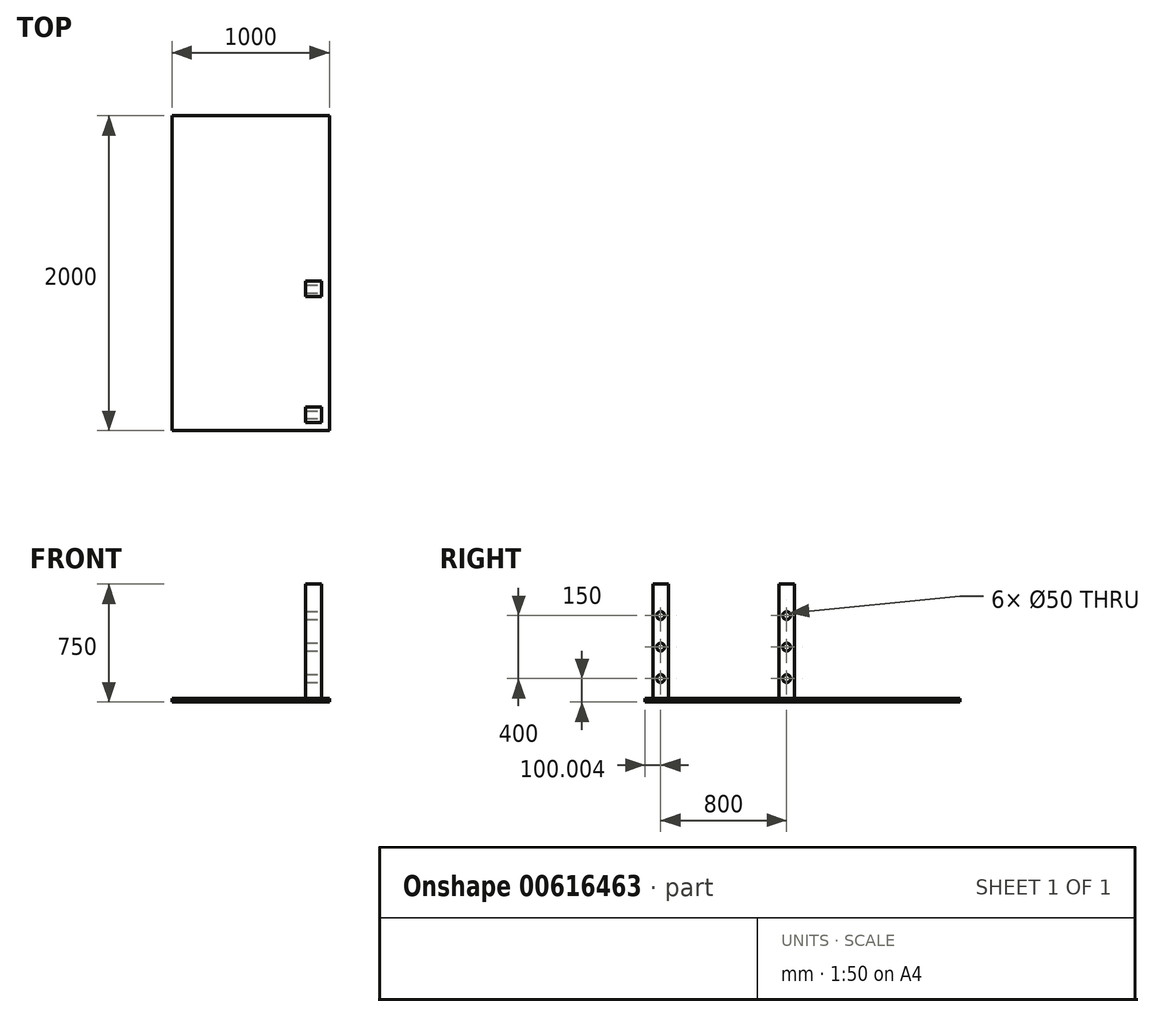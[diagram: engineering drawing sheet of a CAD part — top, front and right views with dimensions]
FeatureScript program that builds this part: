
annotation { "Feature Type Name" : "Feature", "Feature Type Description" : "" }
export const myFeature = defineFeature(function(context is Context, id is Id, definition is map)
    precondition{}
    {
        {
            var Q0;
            Q0=qCreatedBy(makeId("Top.planeOp"),FACE);
            var sketch = newSketch(context, id + "F0", { "sketchPlane" : qUnion([Q0])});
            skLineSegment(sketch, "E0.bottom", {"start": v(503.13, -1003.32) * mm, "end": v(-496.87, -1003.32) * mm});
            skLineSegment(sketch, "E0.top", {"start": v(503.13, 996.68) * mm, "end": v(-496.87, 996.68) * mm});
            skLineSegment(sketch, "E0.left", {"start": v(503.13, -1003.32) * mm, "end": v(503.13, 996.68) * mm});
            skLineSegment(sketch, "E0.right", {"start": v(-496.87, -1003.32) * mm, "end": v(-496.87, 996.68) * mm});
            skPoint(sketch, "E0.middle", {"position": v(3.13, -3.32) * mm});
            skLineSegment(sketch, "E1", {"start": v(-496.87, 996.68) * mm, "end": v(503.13, -1003.32) * mm, "construction": true});
            skSolve(sketch);
        }
        {
            var Q0;
            Q0 = qSketchRegion(id + "F0", true);
            extrude(context, id + "F1", {"entities" : qUnion([Q0]), "depth" : 25 * mm, "offsetDistance" : 25 * mm});
        }
        {
            var Q0;
            Q0=makeQuery(id+"F1.opExtrude","SWEPT_FACE",FACE,{"disambiguationData":[OSD([sQuery(id+"F0.wireOp",EDGE,"E0.left")])]});
            cPlane(context, id + "F2", {"entities" : qUnion([Q0]), "cplaneType" : CPlaneType.OFFSET, "offset" : 50 * mm, "oppositeDirection" : true, "width" : 150 * mm, "height" : 150 * mm});
        }
        {
            var Q0;
            Q0=qCreatedBy(id+"F2.planeOp",FACE);
            var sketch = newSketch(context, id + "F3", { "sketchPlane" : qUnion([Q0])});
            skLineSegment(sketch, "E2.bottom", {"start": v(-953.32, 25) * mm, "end": v(-853.32, 25) * mm});
            skLineSegment(sketch, "E2.top", {"start": v(-953.32, 750) * mm, "end": v(-853.32, 750) * mm});
            skLineSegment(sketch, "E2.left", {"start": v(-953.32, 25) * mm, "end": v(-953.32, 750) * mm});
            skLineSegment(sketch, "E2.right", {"start": v(-853.32, 25) * mm, "end": v(-853.32, 750) * mm});
            skLineSegment(sketch, "E3", {"start": v(-903.32, 750) * mm, "end": v(-903.32, 25) * mm, "construction": true});
            skCircle(sketch, "E4", {"center": v(-903.32, 550) * mm, "radius": 25 * mm});
            skCircle(sketch, "E5", {"center": v(-903.32, 350) * mm, "radius": 25 * mm});
            skCircle(sketch, "E6", {"center": v(-903.32, 150) * mm, "radius": 25 * mm});
            skLineSegment(sketch, "E7.bottom", {"start": v(-153.32, 25) * mm, "end": v(-53.32, 25) * mm});
            skLineSegment(sketch, "E7.top", {"start": v(-153.32, 750) * mm, "end": v(-53.32, 750) * mm});
            skLineSegment(sketch, "E7.left", {"start": v(-153.32, 25) * mm, "end": v(-153.32, 750) * mm});
            skLineSegment(sketch, "E7.right", {"start": v(-53.32, 25) * mm, "end": v(-53.32, 750) * mm});
            skLineSegment(sketch, "E8", {"start": v(-103.32, 750) * mm, "end": v(-103.32, 25) * mm, "construction": true});
            skCircle(sketch, "E9", {"center": v(-103.32, 550) * mm, "radius": 25 * mm});
            skCircle(sketch, "E10", {"center": v(-103.32, 350) * mm, "radius": 25 * mm});
            skCircle(sketch, "E11", {"center": v(-103.32, 150) * mm, "radius": 25 * mm});
            skSolve(sketch);
        }
        {
            var Q0;
            Q0 = qSketchRegion(id + "F3", true);
            extrude(context, id + "F4", {"entities" : qUnion([Q0]), "operationType" : NewBodyOperationType.ADD, "oppositeDirection" : true, "depth" : 100 * mm, "offsetDistance" : 25 * mm});
        }
    });
